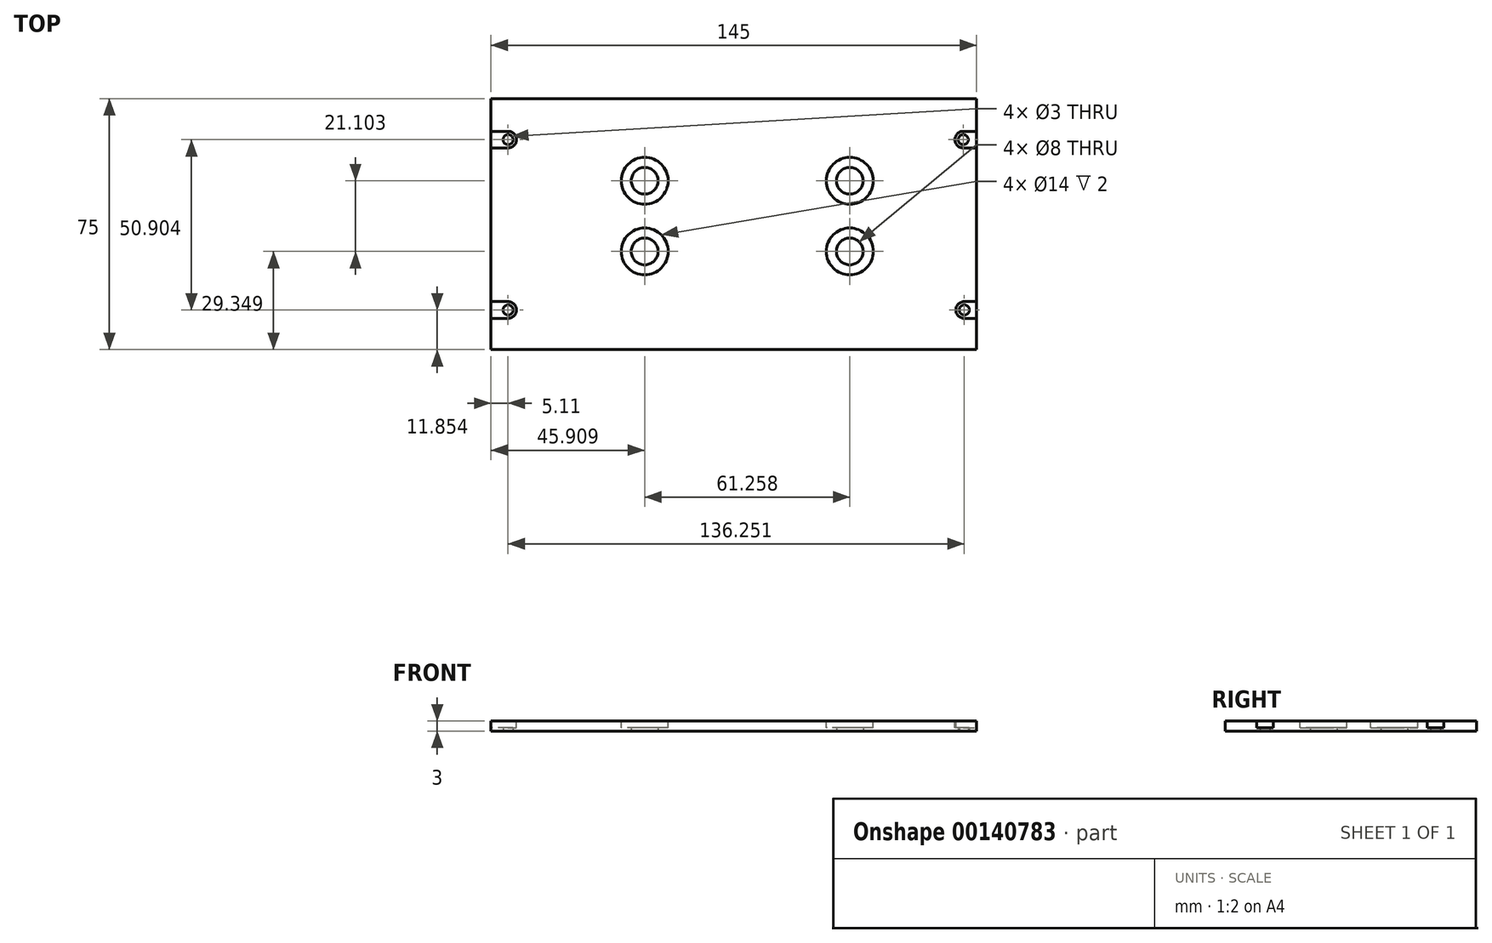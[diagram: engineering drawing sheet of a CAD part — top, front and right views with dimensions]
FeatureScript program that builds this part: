
annotation { "Feature Type Name" : "Feature", "Feature Type Description" : "" }
export const myFeature = defineFeature(function(context is Context, id is Id, definition is map)
    precondition{}
    {
        {
            var Q0;
            Q0=qCreatedBy(makeId("Top.planeOp"),FACE);
            var sketch = newSketch(context, id + "F0", { "sketchPlane" : qUnion([Q0])});
            skLineSegment(sketch, "E0.bottom", {"start": v(0, 0) * mm, "end": v(145, 0) * mm});
            skLineSegment(sketch, "E0.top", {"start": v(0, -75) * mm, "end": v(145, -75) * mm});
            skLineSegment(sketch, "E0.left", {"start": v(0, 0) * mm, "end": v(0, -75) * mm});
            skLineSegment(sketch, "E0.right", {"start": v(145, 0) * mm, "end": v(145, -75) * mm});
            skCircle(sketch, "E1", {"center": v(5.11, -12.24) * mm, "radius": 1.5 * mm});
            skCircle(sketch, "E2", {"center": v(5.11, -63.15) * mm, "radius": 1.5 * mm});
            skCircle(sketch, "E3", {"center": v(141.06, -12.24) * mm, "radius": 1.5 * mm});
            skCircle(sketch, "E4", {"center": v(141.36, -63.15) * mm, "radius": 1.5 * mm});
            skCircle(sketch, "E5", {"center": v(45.9, -24.55) * mm, "radius": 4 * mm});
            skCircle(sketch, "E6", {"center": v(107.17, -24.55) * mm, "radius": 4 * mm});
            skCircle(sketch, "E7", {"center": v(45.9, -45.65) * mm, "radius": 4 * mm});
            skCircle(sketch, "E8", {"center": v(107.17, -45.65) * mm, "radius": 4 * mm});
            skSolve(sketch);
        }
        {
            var Q0;
            Q0=makeQuery(id+"F0.imprint","IMPRINT",FACE,{"disambiguationData":[TD([[makeQuery(id+"F0.imprint","IMPRINT",EDGE,{"derivedFrom":sQuery(id+"F0.wireOp",EDGE,"E0.bottom")}),-1.0]])]});
            extrude(context, id + "F1", {"entities" : qUnion([Q0]), "depth" : 3 * mm});
        }
        {
            var Q0;
            Q0=makeQuery(id+"F1.opExtrude","CAP_FACE",FACE,{"disambiguationData":[OSD([sQuery(id+"F0.wireOp",EDGE,"E0.bottom"),sQuery(id+"F0.wireOp",EDGE,"E0.top"),sQuery(id+"F0.wireOp",EDGE,"E0.left"),sQuery(id+"F0.wireOp",EDGE,"E0.right"),sQuery(id+"F0.wireOp",EDGE,"E1"),sQuery(id+"F0.wireOp",EDGE,"E2"),sQuery(id+"F0.wireOp",EDGE,"E3"),sQuery(id+"F0.wireOp",EDGE,"E4")])],"isStart":false});
            var sketch = newSketch(context, id + "F2", { "sketchPlane" : qUnion([Q0])});
            skArc(sketch, "E9", {"start": v(5.11, -14.74) * mm, "mid": v(7.61, -12.24) * mm, "end": v(5.11, -9.74) * mm});
            skLineSegment(sketch, "E10", {"start": v(5.11, -9.74) * mm, "end": v(-4.9, -9.74) * mm});
            skLineSegment(sketch, "E11", {"start": v(-4.9, -9.74) * mm, "end": v(-4.9, -14.74) * mm});
            skLineSegment(sketch, "E12", {"start": v(5.11, -14.74) * mm, "end": v(-4.9, -14.74) * mm});
            skArc(sketch, "E13", {"start": v(5.11, -65.65) * mm, "mid": v(7.61, -63.15) * mm, "end": v(5.11, -60.65) * mm});
            skLineSegment(sketch, "E14", {"start": v(5.11, -60.65) * mm, "end": v(-4.9, -60.65) * mm});
            skLineSegment(sketch, "E15", {"start": v(-4.9, -60.65) * mm, "end": v(-4.9, -65.65) * mm});
            skLineSegment(sketch, "E16", {"start": v(5.11, -65.65) * mm, "end": v(-4.9, -65.65) * mm});
            skArc(sketch, "E17", {"start": v(141.06, -9.74) * mm, "mid": v(138.56, -12.24) * mm, "end": v(141.06, -14.74) * mm});
            skLineSegment(sketch, "E18", {"start": v(141.06, -9.74) * mm, "end": v(149.46, -9.74) * mm});
            skLineSegment(sketch, "E19", {"start": v(149.46, -9.74) * mm, "end": v(149.46, -14.74) * mm});
            skLineSegment(sketch, "E20", {"start": v(141.06, -14.74) * mm, "end": v(149.46, -14.74) * mm});
            skArc(sketch, "E21", {"start": v(141.36, -60.65) * mm, "mid": v(138.86, -63.15) * mm, "end": v(141.36, -65.65) * mm});
            skLineSegment(sketch, "E22", {"start": v(141.36, -60.65) * mm, "end": v(150.57, -60.65) * mm});
            skLineSegment(sketch, "E23", {"start": v(150.57, -60.65) * mm, "end": v(150.57, -65.65) * mm});
            skLineSegment(sketch, "E24", {"start": v(141.36, -65.65) * mm, "end": v(150.57, -65.65) * mm});
            skCircle(sketch, "E25", {"center": v(45.9, -24.55) * mm, "radius": 7 * mm});
            skCircle(sketch, "E26", {"center": v(45.9, -45.65) * mm, "radius": 7 * mm});
            skCircle(sketch, "E27", {"center": v(107.17, -24.55) * mm, "radius": 7 * mm});
            skCircle(sketch, "E28", {"center": v(107.17, -45.65) * mm, "radius": 7 * mm});
            skSolve(sketch);
        }
        {
            var Q0;
            Q0 = qSketchRegion(id + "F2", true);
            extrude(context, id + "F3", {"entities" : qUnion([Q0]), "operationType" : NewBodyOperationType.REMOVE, "oppositeDirection" : true, "depth" : 2 * mm});
        }
    });
